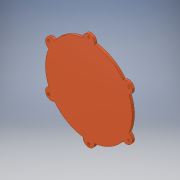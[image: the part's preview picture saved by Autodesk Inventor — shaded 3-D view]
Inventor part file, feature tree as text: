
AUTODESK INVENTOR PART (.ipt)
format: ipt  version: 2017 (Build 210142000, 142)  size: 124,416 bytes
history: native  units: in
note: dims shown in document units (in); Inventor stores cm internally (conversion verified against a paired STEP export)
features: extrude x1, sketch x1
ambient origin geometry x8: Origin, YZ Plane, XZ Plane, XY Plane, X Axis, Y Axis, Z Axis, Center Point
bodies: Solid1 (feature_tree)
feature tree (2):
  extrude  "Extrusion1"  Depth=2.2008in
  sketch  "Sketch2"  dims[d0=0.5906in d7=4.4016in d12=0.1181in d13=2.3622in d15=360.0deg d17=0.1181in d18=0.0in d20=2.2008in d21=0.0394in]
